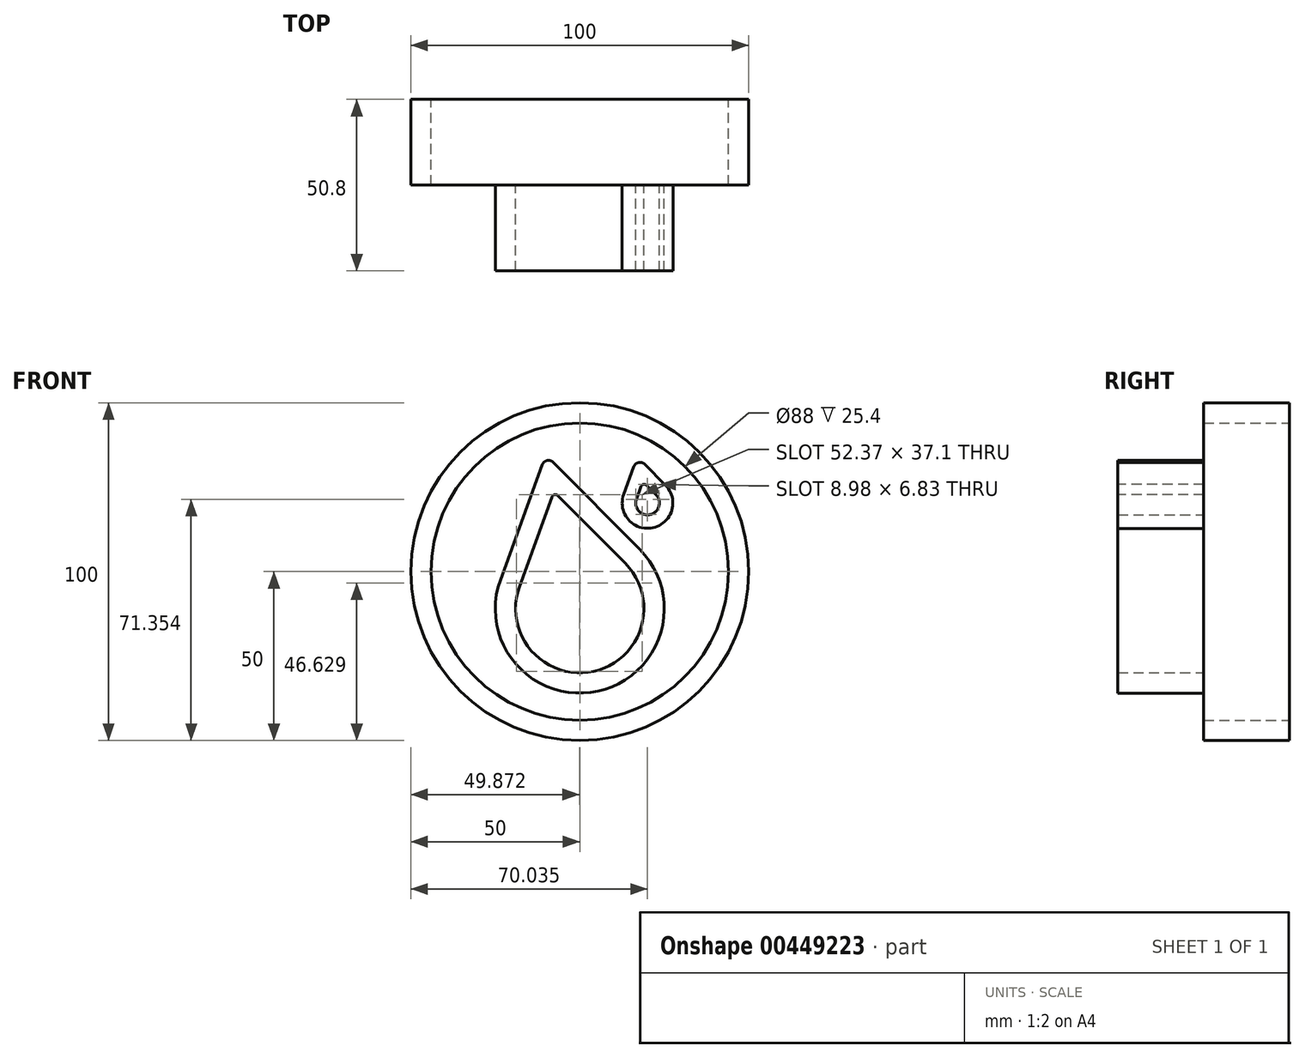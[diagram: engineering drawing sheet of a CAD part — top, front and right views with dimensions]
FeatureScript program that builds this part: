
annotation { "Feature Type Name" : "Feature", "Feature Type Description" : "" }
export const myFeature = defineFeature(function(context is Context, id is Id, definition is map)
    precondition{}
    {
        {
            var Q0;
            Q0=qCreatedBy(makeId("Front.planeOp"),FACE);
            var sketch = newSketch(context, id + "F0", { "sketchPlane" : qUnion([Q0])});
            skCircle(sketch, "E0", {"center": v(0, 0) * mm, "radius": 50 * mm});
            skCircle(sketch, "E1", {"center": v(0, 0) * mm, "radius": 44 * mm});
            skLineSegment(sketch, "E2", {"start": v(0, -40) * mm, "end": v(-28.83, -1.31) * mm});
            skArc(sketch, "E3", {"start": v(0, 8.25) * mm, "mid": v(-21.04, 23.43) * mm, "end": v(-28.83, -1.31) * mm});
            skLineSegment(sketch, "E4", {"start": v(-39.11, 20.16) * mm, "end": v(0, 0) * mm});
            skPoint(sketch, "E5", {"position": v(-30.22, 15.58) * mm});
            skPoint(sketch, "E6", {"position": v(0, -50) * mm});
            skLineSegment(sketch, "E7", {"start": v(-30.22, 15.58) * mm, "end": v(-38.08, 0.33) * mm});
            skLineSegment(sketch, "E8", {"start": v(0, 8.25) * mm, "end": v(0, -40) * mm});
            skLineSegment(sketch, "E9.MirrorCS", {"start": v(0, -40) * mm, "end": v(28.83, -1.31) * mm});
            skArc(sketch, "E10.MirrorCS", {"start": v(0, 8.25) * mm, "mid": v(21.04, 23.43) * mm, "end": v(28.83, -1.31) * mm});
            skArc(sketch, "E11.0", {"start": v(0, 16.5) * mm, "mid": v(25.53, 23.51) * mm, "end": v(30.43, -2.5) * mm});
            skArc(sketch, "E11.1", {"start": v(0, 16.5) * mm, "mid": v(-25.53, 23.51) * mm, "end": v(-30.43, -2.5) * mm});
            skLineSegment(sketch, "E11.2", {"start": v(0, -43.35) * mm, "end": v(-30.43, -2.5) * mm});
            skLineSegment(sketch, "E11.3", {"start": v(0, -43.35) * mm, "end": v(30.43, -2.5) * mm});
            skSolve(sketch);
        }
        {
            var Q0;
            Q0=makeQuery(id+"F0.imprint","IMPRINT",FACE,{"disambiguationData":[TD([[makeQuery(id+"F0.imprint","IMPRINT",EDGE,{"derivedFrom":sQuery(id+"F0.wireOp",EDGE,"E0")}),1.0]])]});
            var Q1;
            {var subQ9=sQuery(id+"F0.wireOp",EDGE,"E2");Q1=makeQuery(id+"F0.imprint","IMPRINT",FACE,{"disambiguationData":[TD([[makeQuery(id+"F0.imprint","IMPRINT",EDGE,{"derivedFrom":subQ9}),1.0]])]});}
            var Q2;
            {var subQ1=sQuery(id+"F0.wireOp",EDGE,"E4");var subQ3=sQuery(id+"F0.wireOp",EDGE,"E11.1");var subQ4=makeQuery(id+"F0.imprint","INTERSECT",VERTEX,{"derivedFrom":[subQ1,subQ3]});Q2=makeQuery(id+"F0.imprint","IMPRINT",FACE,{"disambiguationData":[TD([[makeQuery(id+"F0.imprint","IMPRINT",EDGE,{"disambiguationData":[TD([[subQ4,-1.0]])],"derivedFrom":subQ3}),1.0]])]});}
            extrude(context, id + "F1", {"entities" : qUnion([Q0, Q1, Q2]), "depth" : 25.4 * mm});
        }
        {
            var Q0;
            Q0=makeQuery(id+"F1.opExtrude","SWEPT_EDGE",EDGE,{"disambiguationData":[OSD([sQuery(id+"F0.wireOp",EDGE,"E11.0"),sQuery(id+"F0.wireOp",EDGE,"E11.1")])]});
            fillet(context, id + "F2", {"entities" : qUnion([Q0]), "radius" : 1 * mm, "tangentPropagation" : true, "allowEdgeOverflow" : false});
        }
        {
            var Q0;
            Q0=makeQuery(id+"F1.opExtrude","SWEPT_EDGE",EDGE,{"disambiguationData":[OSD([sQuery(id+"F0.wireOp",EDGE,"E3"),sQuery(id+"F0.wireOp",EDGE,"E8"),sQuery(id+"F0.wireOp",EDGE,"E10.MirrorCS")])]});
            fillet(context, id + "F3", {"entities" : qUnion([Q0]), "radius" : 2 * mm, "tangentPropagation" : true, "allowEdgeOverflow" : false});
        }
        {
            var Q0;
            Q0=makeQuery(id+"F1.opExtrude","SWEPT_EDGE",EDGE,{"disambiguationData":[OSD([sQuery(id+"F0.wireOp",EDGE,"E2"),sQuery(id+"F0.wireOp",EDGE,"E8"),sQuery(id+"F0.wireOp",EDGE,"E9.MirrorCS")])]});
            fillet(context, id + "F4", {"entities" : qUnion([Q0]), "radius" : 1 * mm, "tangentPropagation" : true, "allowEdgeOverflow" : false});
        }
        {
            var Q0;
            Q0=makeQuery(id+"F1.opExtrude","SWEPT_EDGE",EDGE,{"disambiguationData":[OSD([sQuery(id+"F0.wireOp",EDGE,"E11.2"),sQuery(id+"F0.wireOp",EDGE,"E11.3")])]});
            fillet(context, id + "F5", {"entities" : qUnion([Q0]), "radius" : 2 * mm, "tangentPropagation" : true, "allowEdgeOverflow" : false});
        }
        {
            var Q0;
            Q0=makeQuery(id+"F1.opExtrude","SWEPT_BODY",BODY,{"disambiguationData":[OSD([sQuery(id+"F0.wireOp",EDGE,"E2"),sQuery(id+"F0.wireOp",EDGE,"E3"),sQuery(id+"F0.wireOp",EDGE,"E9.MirrorCS"),sQuery(id+"F0.wireOp",EDGE,"E10.MirrorCS"),sQuery(id+"F0.wireOp",EDGE,"E11.0"),sQuery(id+"F0.wireOp",EDGE,"E11.1"),sQuery(id+"F0.wireOp",EDGE,"E11.2"),sQuery(id+"F0.wireOp",EDGE,"E11.3")])]});
            deleteBodies(context, id + "F6", {"entities" : qUnion([Q0])});
        }
        {
            var Q0;
            Q0=makeQuery(id+"F1.opExtrude","CAP_FACE",FACE,{"disambiguationData":[OSD([sQuery(id+"F0.wireOp",EDGE,"E0"),sQuery(id+"F0.wireOp",EDGE,"E1")])],"isStart":false});
            var sketch = newSketch(context, id + "F7", { "sketchPlane" : qUnion([Q0])});
            skArc(sketch, "E12", {"start": v(-7.5, -10) * mm, "mid": v(0, -38) * mm, "end": v(7.5, -10) * mm});
            skPoint(sketch, "E13", {"position": v(0, -38) * mm});
            skArc(sketch, "E14", {"start": v(7.5, 30.5) * mm, "mid": v(0, 38) * mm, "end": v(-7.5, 30.5) * mm});
            skLineSegment(sketch, "E15.left", {"start": v(-7.5, 30.5) * mm, "end": v(-7.5, -10) * mm});
            skLineSegment(sketch, "E15.right", {"start": v(7.5, 30.5) * mm, "end": v(7.5, -10) * mm});
            skPoint(sketch, "E16.orphan", {"position": v(-7.5, -23) * mm});
            skLineSegment(sketch, "E17.0", {"start": v(-9.5, 30.5) * mm, "end": v(-9.5, -8.9) * mm});
            skArc(sketch, "E17.1", {"start": v(9.5, 30.5) * mm, "mid": v(0, 40) * mm, "end": v(-9.5, 30.5) * mm});
            skLineSegment(sketch, "E17.2", {"start": v(9.5, 30.5) * mm, "end": v(9.5, -8.9) * mm});
            skArc(sketch, "E17.3", {"start": v(-9.5, -8.9) * mm, "mid": v(0, -40) * mm, "end": v(9.5, -8.9) * mm});
            skLineSegment(sketch, "E18.0", {"start": v(-5.5, 15) * mm, "end": v(-5.5, -11.22) * mm});
            skArc(sketch, "E18.1", {"start": v(-5.5, -11.22) * mm, "mid": v(0, -36) * mm, "end": v(5.5, -11.22) * mm});
            skLineSegment(sketch, "E18.2", {"start": v(5.5, 15) * mm, "end": v(5.5, -11.22) * mm});
            skLineSegment(sketch, "E19", {"start": v(-5.5, 15) * mm, "end": v(5.5, 15) * mm});
            skLineSegment(sketch, "E20", {"start": v(11.5, 15) * mm, "end": v(26.5, 22.5) * mm});
            skLineSegment(sketch, "E21", {"start": v(26.5, 22.5) * mm, "end": v(26.5, 7.5) * mm});
            skLineSegment(sketch, "E22", {"start": v(26.5, 7.5) * mm, "end": v(11.5, 15) * mm});
            skPoint(sketch, "E23", {"position": v(26.5, 15) * mm});
            skLineSegment(sketch, "E24.0", {"start": v(15.97, 15) * mm, "end": v(24.5, 19.26) * mm});
            skLineSegment(sketch, "E24.1", {"start": v(24.5, 10.74) * mm, "end": v(15.97, 15) * mm});
            skLineSegment(sketch, "E24.2", {"start": v(24.5, 19.26) * mm, "end": v(24.5, 10.74) * mm});
            skSolve(sketch);
        }
        {
            var Q0;
            Q0=qSketchRegion(id+"F7",true);
            var Q1;
            Q1=makeQuery(id+"F7.imprint","IMPRINT",FACE,{"disambiguationData":[TD([[makeQuery(id+"F7.imprint","IMPRINT",EDGE,{"derivedFrom":sQuery(id+"F7.wireOp",EDGE,"E18.0")}),1.0]])]});
            extrude(context, id + "F8", {"entities" : qUnion([Q0, Q1]), "depth" : 25.4 * mm});
        }
        {
            var Q0;
            Q0=makeQuery(id+"F8.opExtrude","SWEPT_EDGE",EDGE,{"disambiguationData":[OSD([sQuery(id+"F7.wireOp",EDGE,"E17.2"),sQuery(id+"F7.wireOp",EDGE,"E17.3")])]});
            var Q1;
            Q1=makeQuery(id+"F8.opExtrude","SWEPT_EDGE",EDGE,{"disambiguationData":[OSD([sQuery(id+"F7.wireOp",EDGE,"E17.0"),sQuery(id+"F7.wireOp",EDGE,"E17.3")])]});
            fillet(context, id + "F9", {"entities" : qUnion([Q0, Q1]), "radius" : 1 * mm, "tangentPropagation" : true, "allowEdgeOverflow" : false});
        }
        {
            var Q0;
            Q0=makeQuery(id+"F8.opExtrude","SWEPT_EDGE",EDGE,{"disambiguationData":[OSD([sQuery(id+"F7.wireOp",EDGE,"E12"),sQuery(id+"F7.wireOp",EDGE,"E15.left")])]});
            var Q1;
            Q1=makeQuery(id+"F8.opExtrude","SWEPT_EDGE",EDGE,{"disambiguationData":[OSD([sQuery(id+"F7.wireOp",EDGE,"E12"),sQuery(id+"F7.wireOp",EDGE,"E15.right")])]});
            fillet(context, id + "F10", {"entities" : qUnion([Q0, Q1]), "radius" : 2 * mm, "tangentPropagation" : true, "allowEdgeOverflow" : false});
        }
        {
            var Q0;
            Q0=makeQuery(id+"F8.opExtrude","SWEPT_EDGE",EDGE,{"disambiguationData":[OSD([sQuery(id+"F7.wireOp",EDGE,"E18.0"),sQuery(id+"F7.wireOp",EDGE,"E18.1")])]});
            var Q1;
            Q1=makeQuery(id+"F8.opExtrude","SWEPT_EDGE",EDGE,{"disambiguationData":[OSD([sQuery(id+"F7.wireOp",EDGE,"E18.1"),sQuery(id+"F7.wireOp",EDGE,"E18.2")])]});
            fillet(context, id + "F11", {"entities" : qUnion([Q0, Q1]), "radius" : 4 * mm, "tangentPropagation" : true, "allowEdgeOverflow" : false});
        }
        {
            var Q0;
            Q0=makeQuery(id+"F8.opExtrude","SWEPT_BODY",BODY,{"disambiguationData":[OSD([sQuery(id+"F7.wireOp",EDGE,"E12"),sQuery(id+"F7.wireOp",EDGE,"E14"),sQuery(id+"F7.wireOp",EDGE,"E15.left"),sQuery(id+"F7.wireOp",EDGE,"E15.right"),sQuery(id+"F7.wireOp",EDGE,"E17.0"),sQuery(id+"F7.wireOp",EDGE,"E17.1"),sQuery(id+"F7.wireOp",EDGE,"E17.2"),sQuery(id+"F7.wireOp",EDGE,"E17.3")])]});
            var Q1;
            Q1=makeQuery(id+"F8.opExtrude","SWEPT_BODY",BODY,{"disambiguationData":[OSD([sQuery(id+"F7.wireOp",EDGE,"E18.0"),sQuery(id+"F7.wireOp",EDGE,"E18.1"),sQuery(id+"F7.wireOp",EDGE,"E18.2"),sQuery(id+"F7.wireOp",EDGE,"E19")])]});
            var Q2;
            Q2=makeQuery(id+"F8.opExtrude","SWEPT_BODY",BODY,{"disambiguationData":[OSD([sQuery(id+"F7.wireOp",EDGE,"E20"),sQuery(id+"F7.wireOp",EDGE,"E21"),sQuery(id+"F7.wireOp",EDGE,"E22"),sQuery(id+"F7.wireOp",EDGE,"E24.0"),sQuery(id+"F7.wireOp",EDGE,"E24.1"),sQuery(id+"F7.wireOp",EDGE,"E24.2")])]});
            deleteBodies(context, id + "F12", {"entities" : qUnion([Q0, Q1, Q2])});
        }
        {
            var Q0;
            Q0=makeQuery(id+"F1.opExtrude","CAP_FACE",FACE,{"disambiguationData":[OSD([sQuery(id+"F0.wireOp",EDGE,"E0"),sQuery(id+"F0.wireOp",EDGE,"E1")])],"isStart":false});
            var sketch = newSketch(context, id + "F13", { "sketchPlane" : qUnion([Q0])});
            skArc(sketch, "E25", {"start": v(-23.5, -2.45) * mm, "mid": v(5.37, -35.42) * mm, "end": v(17.74, 6.61) * mm});
            skLineSegment(sketch, "E26", {"start": v(17.74, 6.61) * mm, "end": v(-10.02, 34.58) * mm});
            skLineSegment(sketch, "E27", {"start": v(-10.02, 34.58) * mm, "end": v(-23.5, -2.45) * mm});
            skPoint(sketch, "E28", {"position": v(0, -36) * mm});
            skLineSegment(sketch, "E29", {"start": v(0, 0) * mm, "end": v(0, 5.34) * mm});
            skArc(sketch, "E30", {"start": v(13.01, 22.85) * mm, "mid": v(21.67, 12.96) * mm, "end": v(25.38, 25.57) * mm});
            skLineSegment(sketch, "E31", {"start": v(13.01, 22.85) * mm, "end": v(17.05, 33.96) * mm});
            skLineSegment(sketch, "E32", {"start": v(17.05, 33.96) * mm, "end": v(25.38, 25.57) * mm});
            skLineSegment(sketch, "E33.0", {"start": v(13.49, 2.38) * mm, "end": v(-7.61, 23.64) * mm});
            skArc(sketch, "E33.1", {"start": v(-17.85, -4.5) * mm, "mid": v(4.08, -29.56) * mm, "end": v(13.49, 2.38) * mm});
            skLineSegment(sketch, "E33.2", {"start": v(-7.61, 23.64) * mm, "end": v(-17.85, -4.5) * mm});
            skLineSegment(sketch, "E34.0", {"start": v(16.77, 21.48) * mm, "end": v(18.66, 26.67) * mm});
            skArc(sketch, "E34.1", {"start": v(16.77, 21.48) * mm, "mid": v(20.8, 16.87) * mm, "end": v(22.54, 22.75) * mm});
            skLineSegment(sketch, "E34.2", {"start": v(18.66, 26.67) * mm, "end": v(22.54, 22.75) * mm});
            skSolve(sketch);
        }
        {
            var Q0;
            Q0=makeQuery(id+"F13.imprint","IMPRINT",FACE,{"disambiguationData":[TD([[makeQuery(id+"F13.imprint","IMPRINT",EDGE,{"derivedFrom":sQuery(id+"F13.wireOp",EDGE,"E25")}),1.0]])]});
            var Q1;
            Q1=makeQuery(id+"F13.imprint","IMPRINT",FACE,{"disambiguationData":[TD([[makeQuery(id+"F13.imprint","IMPRINT",EDGE,{"derivedFrom":sQuery(id+"F13.wireOp",EDGE,"E30")}),1.0]])]});
            extrude(context, id + "F14", {"entities" : qUnion([Q0, Q1]), "depth" : 25.4 * mm});
        }
        {
            var Q0;
            Q0=makeQuery(id+"F14.opExtrude","SWEPT_EDGE",EDGE,{"disambiguationData":[OSD([sQuery(id+"F13.wireOp",EDGE,"E33.0"),sQuery(id+"F13.wireOp",EDGE,"E33.2")])]});
            var Q1;
            Q1=makeQuery(id+"F14.opExtrude","SWEPT_EDGE",EDGE,{"disambiguationData":[OSD([sQuery(id+"F13.wireOp",EDGE,"E34.0"),sQuery(id+"F13.wireOp",EDGE,"E34.2")])]});
            fillet(context, id + "F15", {"entities" : qUnion([Q0, Q1]), "radius" : 1 * mm, "tangentPropagation" : true, "allowEdgeOverflow" : false});
        }
        {
            var Q0;
            Q0=makeQuery(id+"F14.opExtrude","SWEPT_EDGE",EDGE,{"disambiguationData":[OSD([sQuery(id+"F13.wireOp",EDGE,"E26"),sQuery(id+"F13.wireOp",EDGE,"E27")])]});
            var Q1;
            Q1=makeQuery(id+"F14.opExtrude","SWEPT_EDGE",EDGE,{"disambiguationData":[OSD([sQuery(id+"F13.wireOp",EDGE,"E31"),sQuery(id+"F13.wireOp",EDGE,"E32")])]});
            fillet(context, id + "F16", {"entities" : qUnion([Q0, Q1]), "radius" : 2 * mm, "tangentPropagation" : true, "allowEdgeOverflow" : false});
        }
    });
